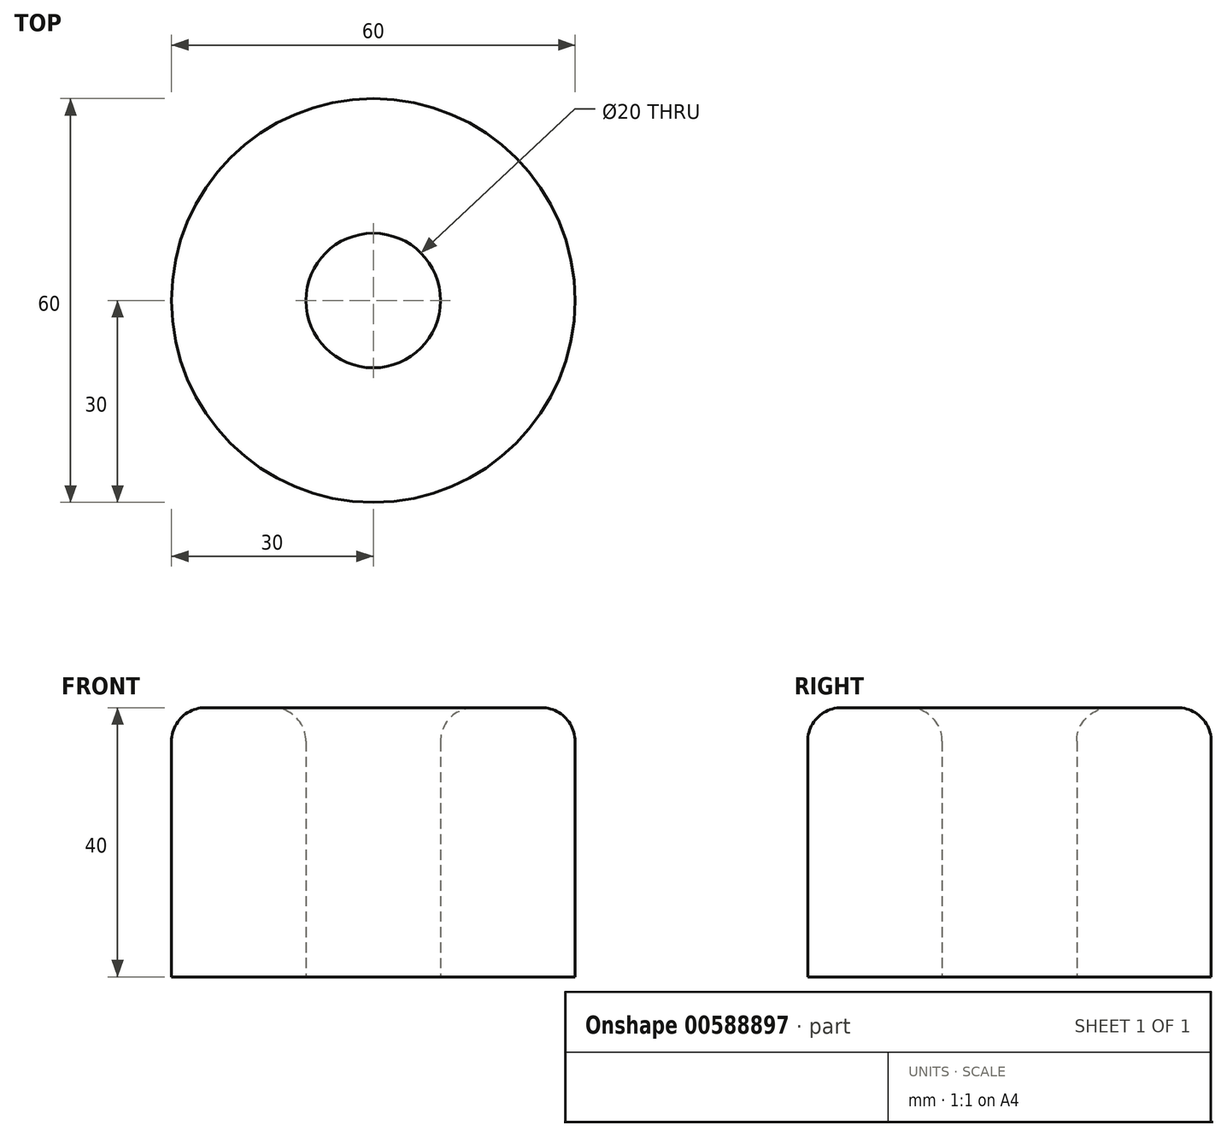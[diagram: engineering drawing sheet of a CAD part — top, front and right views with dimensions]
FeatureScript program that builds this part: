
annotation { "Feature Type Name" : "Feature", "Feature Type Description" : "" }
export const myFeature = defineFeature(function(context is Context, id is Id, definition is map)
    precondition{}
    {
        {
            var Q0;
            Q0=qCreatedBy(makeId("Top.planeOp"),FACE);
            var sketch = newSketch(context, id + "F0", { "sketchPlane" : qUnion([Q0])});
            skCircle(sketch, "E0", {"center": v(0, 0) * mm, "radius": 30 * mm});
            skCircle(sketch, "E1.0", {"center": v(0, 0) * mm, "radius": 10 * mm});
            skSolve(sketch);
        }
        {
            var Q0;
            Q0 = qSketchRegion(id + "F0", true);
            extrude(context, id + "F1", {"entities" : qUnion([Q0]), "depth" : 40 * mm, "offsetDistance" : 25 * mm});
        }
        {
            var Q0;
            Q0=makeQuery(id+"F1.opExtrude","CAP_EDGE",EDGE,{"disambiguationData":[OSD([sQuery(id+"F0.wireOp",EDGE,"E0")])],"isStart":false});
            var Q1;
            Q1=makeQuery(id+"F1.opExtrude","CAP_EDGE",EDGE,{"disambiguationData":[OSD([sQuery(id+"F0.wireOp",EDGE,"E1.0")])],"isStart":false});
            fillet(context, id + "F2", {"entities" : qUnion([Q0, Q1]), "radius" : 5 * mm, "tangentPropagation" : true, "allowEdgeOverflow" : false});
        }
    });
